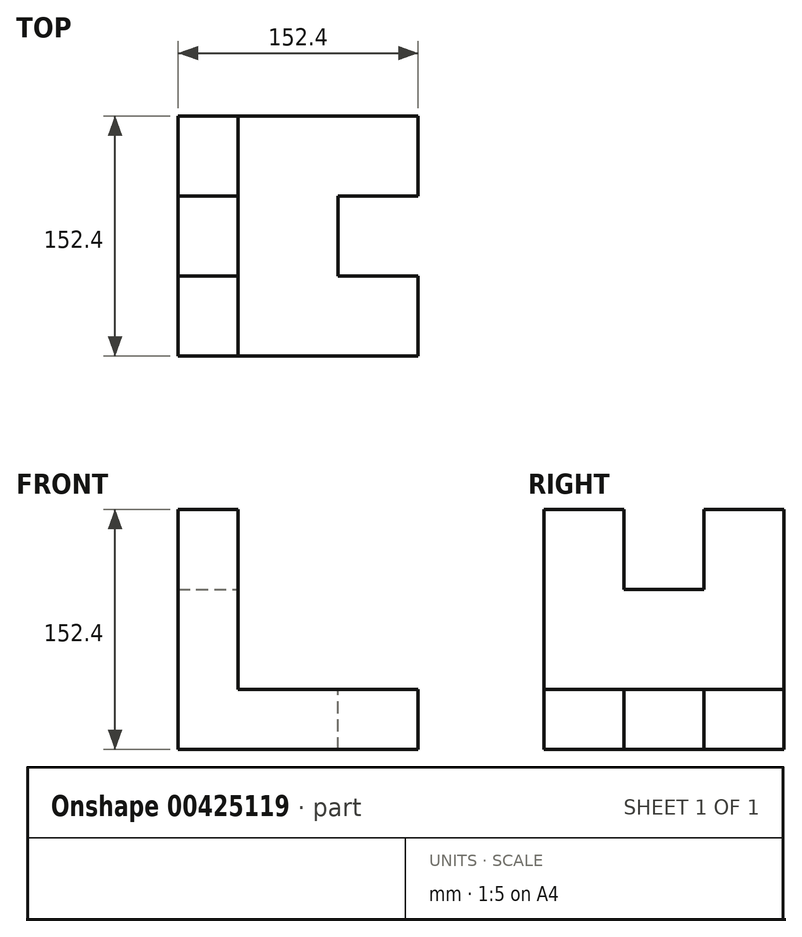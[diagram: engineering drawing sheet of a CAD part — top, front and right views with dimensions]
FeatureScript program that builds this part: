
annotation { "Feature Type Name" : "Feature", "Feature Type Description" : "" }
export const myFeature = defineFeature(function(context is Context, id is Id, definition is map)
    precondition{}
    {
        {
            var Q0;
            Q0=qCreatedBy(makeId("Front.planeOp"),FACE);
            var sketch = newSketch(context, id + "F0", { "sketchPlane" : qUnion([Q0])});
            skLineSegment(sketch, "E0.bottom", {"start": v(0, 0) * mm, "end": v(152.4, 0) * mm});
            skLineSegment(sketch, "E0.top", {"start": v(0, 152.4) * mm, "end": v(152.4, 152.4) * mm});
            skLineSegment(sketch, "E0.left", {"start": v(0, 0) * mm, "end": v(0, 152.4) * mm});
            skLineSegment(sketch, "E0.right", {"start": v(152.4, 0) * mm, "end": v(152.4, 152.4) * mm});
            skSolve(sketch);
        }
        {
            var Q0;
            Q0 = qSketchRegion(id + "F0", true);
            extrude(context, id + "F1", {"entities" : qUnion([Q0]), "depth" : 152.4 * mm});
        }
        {
            var Q0;
            Q0=makeQuery(id+"F1.opExtrude","CAP_FACE",FACE,{"disambiguationData":[OSD([sQuery(id+"F0.wireOp",EDGE,"E0.bottom"),sQuery(id+"F0.wireOp",EDGE,"E0.top"),sQuery(id+"F0.wireOp",EDGE,"E0.left"),sQuery(id+"F0.wireOp",EDGE,"E0.right")])],"isStart":false});
            var sketch = newSketch(context, id + "F2", { "sketchPlane" : qUnion([Q0])});
            skLineSegment(sketch, "E1.bottom", {"start": v(152.4, 152.4) * mm, "end": v(38.1, 152.4) * mm});
            skLineSegment(sketch, "E1.top", {"start": v(152.4, 38.1) * mm, "end": v(38.1, 38.1) * mm});
            skLineSegment(sketch, "E1.left", {"start": v(152.4, 152.4) * mm, "end": v(152.4, 38.1) * mm});
            skLineSegment(sketch, "E1.right", {"start": v(38.1, 152.4) * mm, "end": v(38.1, 38.1) * mm});
            skSolve(sketch);
        }
        {
            var Q0;
            Q0 = qSketchRegion(id + "F2", true);
            extrude(context, id + "F3", {"entities" : qUnion([Q0]), "operationType" : NewBodyOperationType.REMOVE, "oppositeDirection" : true, "depth" : 152.4 * mm});
        }
        {
            var Q0;
            Q0=makeQuery(id+"F3.boolean.opBoolean","COPY",FACE,{"derivedFrom":makeQuery(id+"F3.opExtrude","SWEPT_FACE",FACE,{"disambiguationData":[OSD([sQuery(id+"F2.wireOp",EDGE,"E1.top")])]})});
            var sketch = newSketch(context, id + "F4", { "sketchPlane" : qUnion([Q0])});
            skPoint(sketch, "E2", {"position": v(152.4, -76.2) * mm});
            skLineSegment(sketch, "E3.bottom", {"start": v(203.2, -50.8) * mm, "end": v(101.6, -50.8) * mm});
            skLineSegment(sketch, "E3.top", {"start": v(203.2, -101.6) * mm, "end": v(101.6, -101.6) * mm});
            skLineSegment(sketch, "E3.left", {"start": v(203.2, -50.8) * mm, "end": v(203.2, -101.6) * mm});
            skLineSegment(sketch, "E3.right", {"start": v(101.6, -50.8) * mm, "end": v(101.6, -101.6) * mm});
            skSolve(sketch);
        }
        {
            var Q0;
            Q0 = qSketchRegion(id + "F4", true);
            extrude(context, id + "F5", {"entities" : qUnion([Q0]), "operationType" : NewBodyOperationType.REMOVE, "oppositeDirection" : true, "depth" : 127 * mm});
        }
        {
            var Q0;
            Q0=makeQuery(id+"F3.boolean.opBoolean","COPY",FACE,{"derivedFrom":makeQuery(id+"F3.opExtrude","SWEPT_FACE",FACE,{"disambiguationData":[OSD([sQuery(id+"F2.wireOp",EDGE,"E1.right")])]})});
            var sketch = newSketch(context, id + "F6", { "sketchPlane" : qUnion([Q0])});
            skPoint(sketch, "E4", {"position": v(-76.2, 152.4) * mm});
            skLineSegment(sketch, "E5.bottom", {"start": v(-50.8, 101.6) * mm, "end": v(-101.6, 101.6) * mm});
            skLineSegment(sketch, "E5.top", {"start": v(-50.8, 203.2) * mm, "end": v(-101.6, 203.2) * mm});
            skLineSegment(sketch, "E5.left", {"start": v(-50.8, 101.6) * mm, "end": v(-50.8, 203.2) * mm});
            skLineSegment(sketch, "E5.right", {"start": v(-101.6, 101.6) * mm, "end": v(-101.6, 203.2) * mm});
            skSolve(sketch);
        }
        {
            var Q0;
            Q0 = qSketchRegion(id + "F6", true);
            extrude(context, id + "F7", {"entities" : qUnion([Q0]), "operationType" : NewBodyOperationType.REMOVE, "oppositeDirection" : true, "depth" : 127 * mm});
        }
    });
